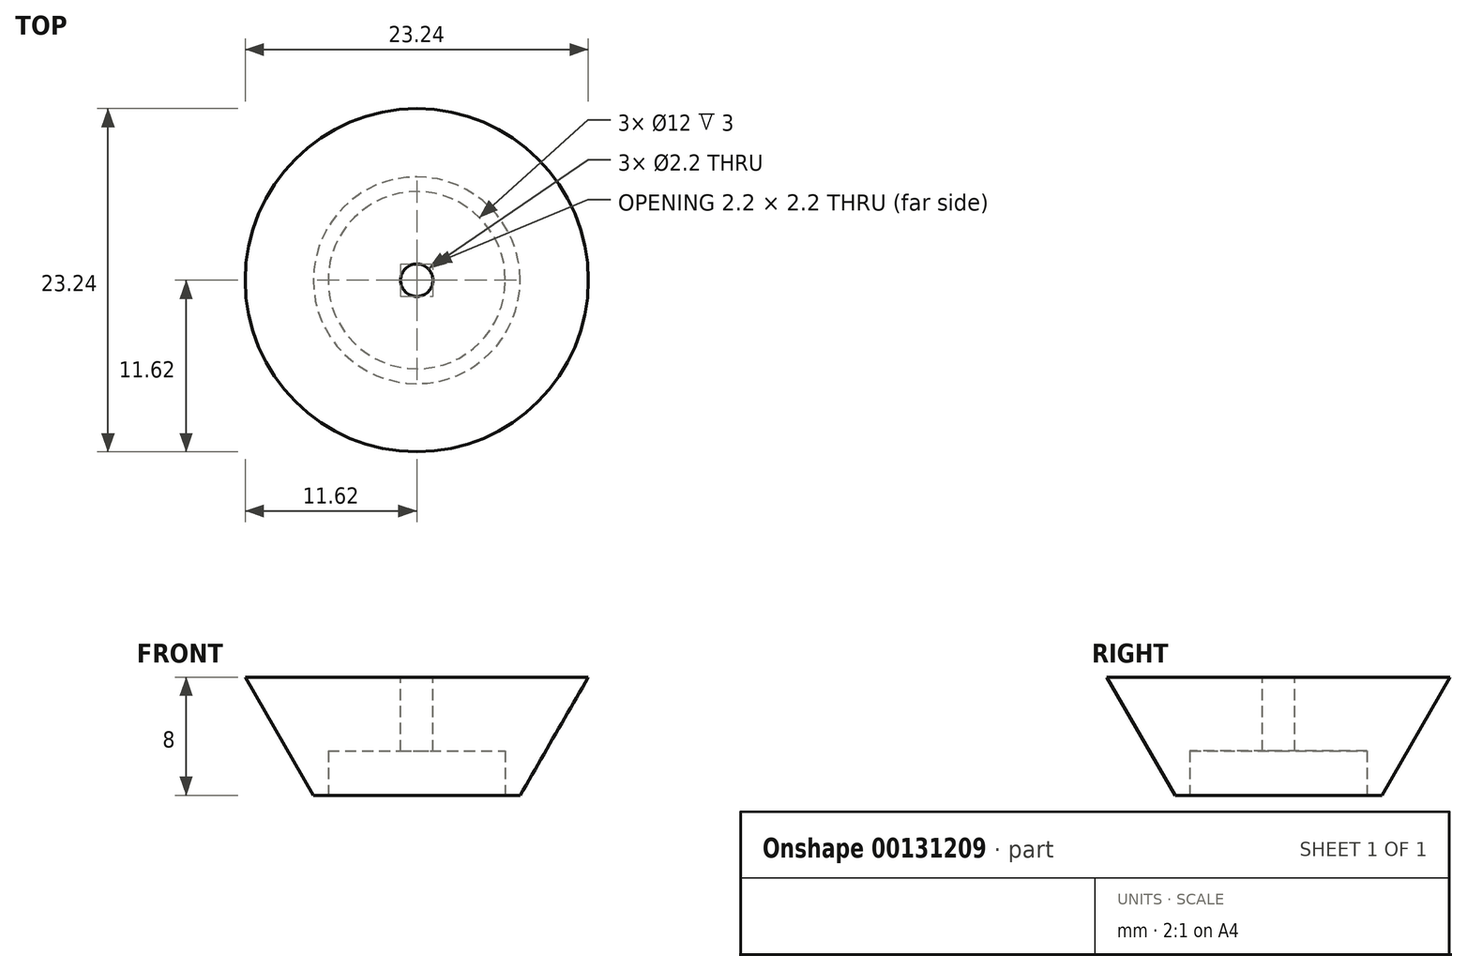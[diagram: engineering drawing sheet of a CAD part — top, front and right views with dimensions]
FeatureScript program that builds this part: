
annotation { "Feature Type Name" : "Feature", "Feature Type Description" : "" }
export const myFeature = defineFeature(function(context is Context, id is Id, definition is map)
    precondition{}
    {
        {
            var Q0;
            Q0=qCreatedBy(makeId("Top.planeOp"),FACE);
            var sketch = newSketch(context, id + "F0", { "sketchPlane" : qUnion([Q0])});
            skCircle(sketch, "E0", {"center": v(0, 0) * mm, "radius": 7 * mm});
            skSolve(sketch);
        }
        {
            var Q0;
            Q0 = qSketchRegion(id + "F0", true);
            extrude(context, id + "F1", {"entities" : qUnion([Q0]), "depth" : 8 * mm, "hasDraft" : true, "draftAngle" : 30 * degree});
        }
        {
            var Q0;
            Q0=makeQuery(id+"F1.opExtrude","CAP_FACE",FACE,{"disambiguationData":[OSD([sQuery(id+"F0.wireOp",EDGE,"E0")])],"isStart":true});
            var sketch = newSketch(context, id + "F2", { "sketchPlane" : qUnion([Q0])});
            skCircle(sketch, "E1", {"center": v(0, 0) * mm, "radius": 6 * mm});
            skSolve(sketch);
        }
        {
            var Q0;
            Q0 = qSketchRegion(id + "F2", true);
            extrude(context, id + "F3", {"entities" : qUnion([Q0]), "operationType" : NewBodyOperationType.REMOVE, "oppositeDirection" : true, "depth" : 3 * mm});
        }
        {
            var Q0;
            Q0=makeQuery(id+"F1.opExtrude","CAP_FACE",FACE,{"disambiguationData":[OSD([sQuery(id+"F0.wireOp",EDGE,"E0")])],"isStart":false});
            var sketch = newSketch(context, id + "F4", { "sketchPlane" : qUnion([Q0])});
            skCircle(sketch, "E2", {"center": v(0, 0) * mm, "radius": 1.1 * mm});
            skSolve(sketch);
        }
        {
            var Q0;
            Q0 = qSketchRegion(id + "F4", true);
            extrude(context, id + "F5", {"entities" : qUnion([Q0]), "operationType" : NewBodyOperationType.REMOVE, "oppositeDirection" : true, "depth" : 25 * mm});
        }
    });
